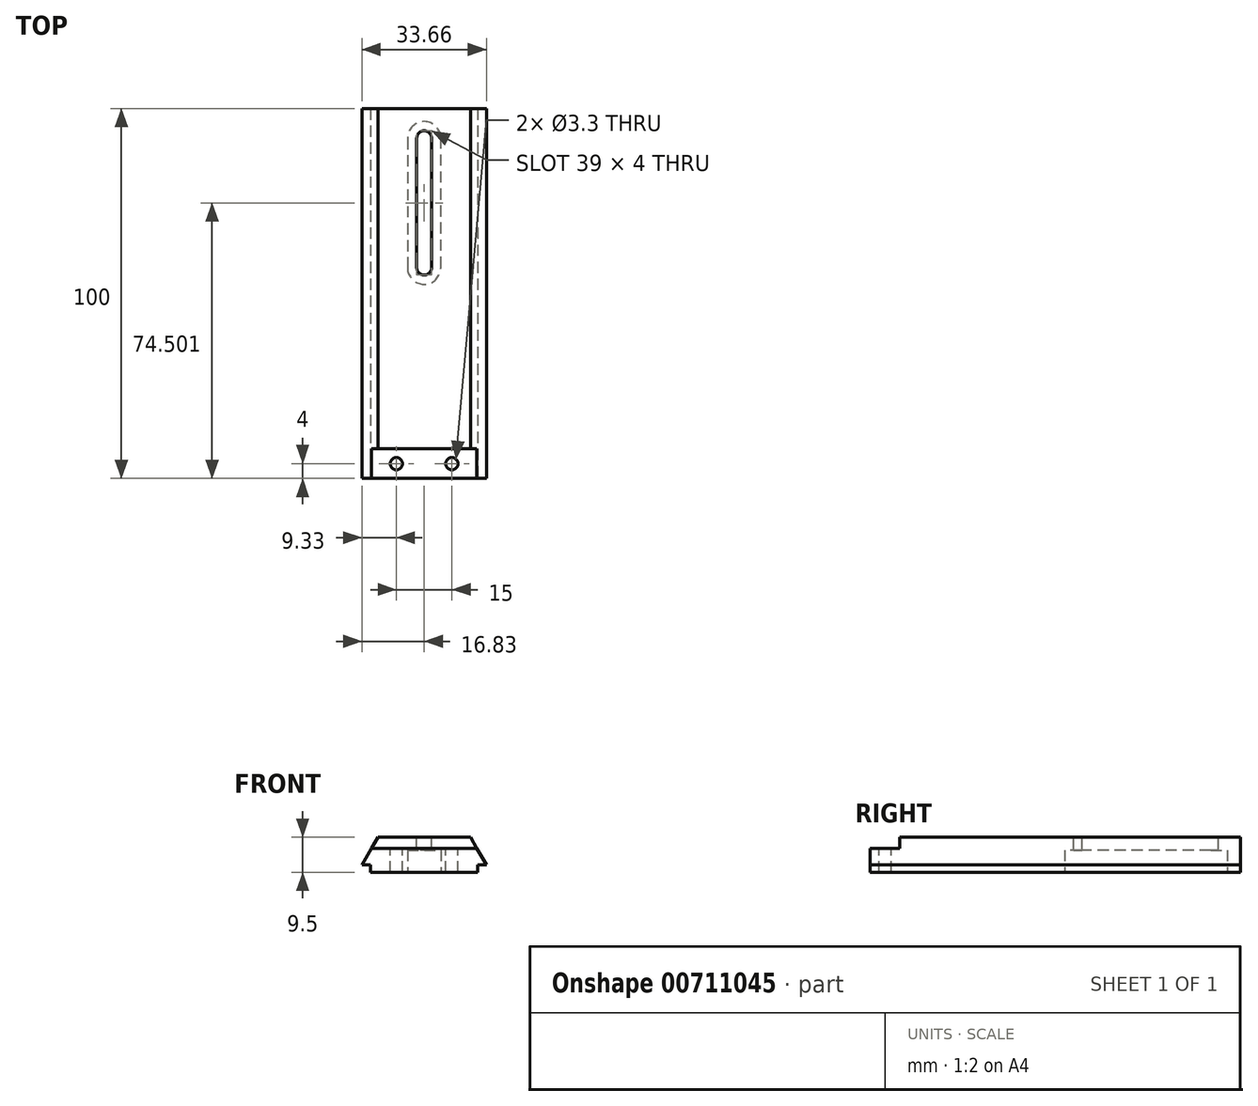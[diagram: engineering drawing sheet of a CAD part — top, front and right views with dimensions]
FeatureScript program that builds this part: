
annotation { "Feature Type Name" : "Feature", "Feature Type Description" : "" }
export const myFeature = defineFeature(function(context is Context, id is Id, definition is map)
    precondition{}
    {
        {
            var Q0;
            Q0=qCreatedBy(makeId("Front.planeOp"),FACE);
            var sketch = newSketch(context, id + "F0", { "sketchPlane" : qUnion([Q0])});
            skLineSegment(sketch, "E0", {"start": v(-14.5, 2) * mm, "end": v(-16.83, 2) * mm});
            skLineSegment(sketch, "E1", {"start": v(-16.83, 2) * mm, "end": v(-12.5, 9.5) * mm});
            skLineSegment(sketch, "E2", {"start": v(14.5, 2) * mm, "end": v(16.83, 2) * mm});
            skLineSegment(sketch, "E3", {"start": v(16.83, 2) * mm, "end": v(12.5, 9.5) * mm});
            skLineSegment(sketch, "E4", {"start": v(-12.5, 9.5) * mm, "end": v(12.5, 9.5) * mm});
            skLineSegment(sketch, "E5", {"start": v(14.5, 2) * mm, "end": v(14.5, 0) * mm});
            skLineSegment(sketch, "E6", {"start": v(-14.5, 2) * mm, "end": v(-14.5, 0) * mm});
            skLineSegment(sketch, "E7", {"start": v(14.5, 0) * mm, "end": v(-14.5, 0) * mm});
            skLineSegment(sketch, "E8", {"start": v(0, 0) * mm, "end": v(0, 14.15) * mm, "construction": true});
            skSolve(sketch);
        }
        {
            var Q0;
            Q0=makeQuery(id+"F0.imprint","IMPRINT",FACE,{"disambiguationData":[TD([[makeQuery(id+"F0.imprint","IMPRINT",EDGE,{"derivedFrom":sQuery(id+"F0.wireOp",EDGE,"E0")}),-1.0]])]});
            extrude(context, id + "F1", {"entities" : qUnion([Q0]), "endBound" : BoundingType.SYMMETRIC, "oppositeDirection" : true, "depth" : 100 * mm, "offsetDistance" : 25 * mm});
        }
        {
            var Q0;
            Q0=makeQuery(id+"F1.opExtrude","SWEPT_FACE",FACE,{"disambiguationData":[OSD([sQuery(id+"F0.wireOp",EDGE,"E7")])]});
            var sketch = newSketch(context, id + "F2", { "sketchPlane" : qUnion([Q0])});
            skLineSegment(sketch, "E9", {"start": v(0, 0) * mm, "end": v(0, -50) * mm, "construction": true});
            skArc(sketch, "E10", {"start": v(4.5, -7) * mm, "mid": v(0, -2.5) * mm, "end": v(-4.5, -7) * mm});
            skLineSegment(sketch, "E11", {"start": v(4.5, -7) * mm, "end": v(4.5, -42) * mm});
            skLineSegment(sketch, "E12", {"start": v(-4.5, -42) * mm, "end": v(-4.5, -7) * mm});
            skArc(sketch, "E13", {"start": v(-4.5, -42) * mm, "mid": v(0, -46.5) * mm, "end": v(4.5, -42) * mm});
            skSolve(sketch);
        }
        {
            var Q0;
            Q0=makeQuery(id+"F2.imprint","IMPRINT",FACE,{"disambiguationData":[TD([[makeQuery(id+"F2.imprint","IMPRINT",EDGE,{"derivedFrom":sQuery(id+"F2.wireOp",EDGE,"E10")}),1.0]])]});
            var Q1;
            Q1=makeQuery(id+"F1.opExtrude","SWEPT_FACE",FACE,{"disambiguationData":[OSD([sQuery(id+"F0.wireOp",EDGE,"E4")])]});
            extrude(context, id + "F3", {"entities" : qUnion([Q0, Q1]), "operationType" : NewBodyOperationType.REMOVE, "oppositeDirection" : true, "depth" : 6 * mm, "offsetDistance" : 25 * mm});
        }
        {
            var Q0;
            Q0=makeQuery(id+"F1.opExtrude","SWEPT_FACE",FACE,{"disambiguationData":[OSD([sQuery(id+"F0.wireOp",EDGE,"E4")])]});
            var sketch = newSketch(context, id + "F4", { "sketchPlane" : qUnion([Q0])});
            skLineSegment(sketch, "E14.0.0", {"start": v(-4.5, 7) * mm, "end": v(-4.5, 42) * mm, "construction": true});
            skArc(sketch, "E14.0.1", {"start": v(-4.5, 42) * mm, "mid": v(-4.5, 42) * mm, "end": v(-4.5, 42) * mm, "construction": true});
            skArc(sketch, "E14.0.2", {"start": v(-4.5, 42) * mm, "mid": v(0, 46.5) * mm, "end": v(4.5, 42) * mm, "construction": true});
            skLineSegment(sketch, "E14.0.3", {"start": v(4.5, 42) * mm, "end": v(4.5, 7) * mm, "construction": true});
            skArc(sketch, "E14.0.4", {"start": v(4.5, 7) * mm, "mid": v(0, 2.5) * mm, "end": v(-4.5, 7) * mm, "construction": true});
            skCircle(sketch, "E15", {"center": v(0, 42) * mm, "radius": 2 * mm});
            skCircle(sketch, "E16", {"center": v(0, 7) * mm, "radius": 2 * mm});
            skLineSegment(sketch, "E17", {"start": v(2, 42) * mm, "end": v(2, 7) * mm});
            skLineSegment(sketch, "E18", {"start": v(-2, 7.2) * mm, "end": v(-2, 42) * mm});
            skSolve(sketch);
        }
        {
            var Q0;
            {var subQ0=sQuery(id+"F4.wireOp",EDGE,"E16");var subQ1=makeQuery(id+"F4.imprint","INTERSECT",VERTEX,{"derivedFrom":[subQ0,sQuery(id+"F4.wireOp",EDGE,"E17")]});Q0=makeQuery(id+"F4.imprint","IMPRINT",FACE,{"disambiguationData":[TD([[makeQuery(id+"F4.imprint","IMPRINT",EDGE,{"disambiguationData":[TD([[subQ1,-1.0]])],"derivedFrom":subQ0}),1.0]])]});}
            var Q1;
            {var subQ0=sQuery(id+"F4.wireOp",EDGE,"E17");Q1=makeQuery(id+"F4.imprint","IMPRINT",FACE,{"disambiguationData":[TD([[makeQuery(id+"F4.imprint","IMPRINT",EDGE,{"derivedFrom":subQ0}),-1.0]])]});}
            var Q2;
            {var subQ0=sQuery(id+"F4.wireOp",EDGE,"E15");var subQ1=makeQuery(id+"F4.imprint","INTERSECT",VERTEX,{"derivedFrom":[subQ0,sQuery(id+"F4.wireOp",EDGE,"E17")]});Q2=makeQuery(id+"F4.imprint","IMPRINT",FACE,{"disambiguationData":[TD([[makeQuery(id+"F4.imprint","IMPRINT",EDGE,{"disambiguationData":[TD([[subQ1,-1.0]])],"derivedFrom":subQ0}),1.0]])]});}
            extrude(context, id + "F5", {"entities" : qUnion([Q0, Q1, Q2]), "operationType" : NewBodyOperationType.REMOVE, "oppositeDirection" : true, "depth" : 25 * mm, "offsetDistance" : 25 * mm});
        }
        {
            var Q0;
            Q0=makeQuery(id+"F1.opExtrude","SWEPT_FACE",FACE,{"disambiguationData":[OSD([sQuery(id+"F0.wireOp",EDGE,"E4")])]});
            var sketch = newSketch(context, id + "F6", { "sketchPlane" : qUnion([Q0])});
            skLineSegment(sketch, "E19.bottom", {"start": v(24.05, -55.52) * mm, "end": v(-23.78, -55.52) * mm});
            skLineSegment(sketch, "E19.top", {"start": v(24.05, -42) * mm, "end": v(-23.78, -42) * mm});
            skLineSegment(sketch, "E19.left", {"start": v(24.05, -55.52) * mm, "end": v(24.05, -42) * mm});
            skLineSegment(sketch, "E19.right", {"start": v(-23.78, -55.52) * mm, "end": v(-23.78, -42) * mm});
            skSolve(sketch);
        }
        {
            var Q0;
            {var subQ1=sQuery(id+"F0.wireOp",EDGE,"E4");var subQ6=makeQuery(id+"F1.opExtrude","CAP_EDGE",EDGE,{"disambiguationData":[OSD([subQ1])],"isStart":true});Q0=makeQuery(id+"F6.imprint","IMPRINT",FACE,{"disambiguationData":[TD([[makeQuery(id+"F6.imprint","IMPRINT",EDGE,{"derivedFrom":subQ6}),1.0]])]});}
            var Q1;
            Q1=makeQuery(id+"F6.imprint","IMPRINT",FACE,{"disambiguationData":[TD([[makeQuery(id+"F6.imprint","IMPRINT",EDGE,{"derivedFrom":sQuery(id+"F6.wireOp",EDGE,"E19.bottom")}),-1.0]])]});
            extrude(context, id + "F7", {"entities" : qUnion([Q0, Q1]), "operationType" : NewBodyOperationType.REMOVE, "oppositeDirection" : true, "depth" : 3 * mm, "offsetDistance" : 25 * mm});
        }
        {
            var Q0;
            Q0=makeQuery(id+"F7.boolean.opBoolean","COPY",FACE,{"derivedFrom":makeQuery(id+"F7.opExtrude","CAP_FACE",FACE,{"disambiguationData":[OSD([sQuery(id+"F6.wireOp",EDGE,"E19.bottom"),sQuery(id+"F6.wireOp",EDGE,"E19.top"),sQuery(id+"F6.wireOp",EDGE,"E19.left"),sQuery(id+"F6.wireOp",EDGE,"E19.right")])],"isStart":false})});
            var sketch = newSketch(context, id + "F8", { "sketchPlane" : qUnion([Q0])});
            skLineSegment(sketch, "E20", {"start": v(-14.23, -46) * mm, "end": v(14.23, -46) * mm, "construction": true});
            skPoint(sketch, "E21", {"position": v(-7.5, -46) * mm});
            skPoint(sketch, "E22", {"position": v(7.5, -46) * mm});
            skLineSegment(sketch, "E23", {"start": v(0, 0) * mm, "end": v(0, -56.93) * mm, "construction": true});
            skPoint(sketch, "E23.endSnap0", {"position": v(0, -50) * mm});
            skSolve(sketch);
        }
        {
            var Q0;
            Q0=sQuery(id+"F8.wireOp",VERTEX,"E21");
            var Q1;
            Q1=sQuery(id+"F8.wireOp",VERTEX,"E22");
            var Q2;
            Q2=makeQuery(id+"F1.opExtrude","SWEPT_BODY",BODY,{"disambiguationData":[OSD([sQuery(id+"F0.wireOp",EDGE,"E0"),sQuery(id+"F0.wireOp",EDGE,"E1"),sQuery(id+"F0.wireOp",EDGE,"E2"),sQuery(id+"F0.wireOp",EDGE,"E3"),sQuery(id+"F0.wireOp",EDGE,"E4"),sQuery(id+"F0.wireOp",EDGE,"E5"),sQuery(id+"F0.wireOp",EDGE,"E6"),sQuery(id+"F0.wireOp",EDGE,"E7")])]});
            hole(context, id + "F9", {"style" : HoleStyle.SIMPLE, "endStyle" : HoleEndStyle.THROUGH, "standardTappedOrClearance" : lookupTablePath({ "standard" : "ISO", "engagement" : "75%", "pitch" : "0.7 mm", "size" : "M4", "type" : "Tapped" }), "standardBlindInLast" : lookupTablePath({ "standard" : "ISO", "engagement" : "75%", "pitch" : "0.7 mm", "size" : "M4", "type" : "Tapped" }), "holeDiameter" : 3.3 * mm, "majorDiameter" : 4 * mm, "showTappedDepth" : true, "isTappedThrough" : true, "tappedDepth" : 12 * mm, "tapClearance" : 3, "locations" : qUnion([Q0, Q1]), "scope" : qUnion([Q2])});
        }
    });
